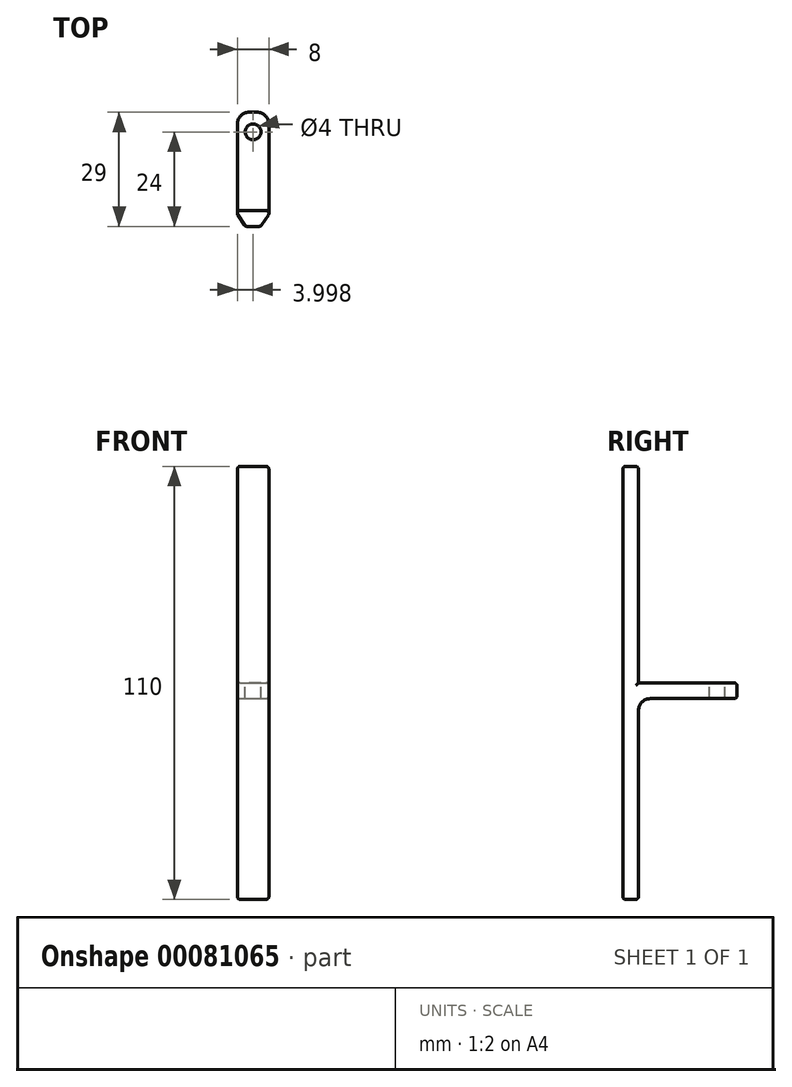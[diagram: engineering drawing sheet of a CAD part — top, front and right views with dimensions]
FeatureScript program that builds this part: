
annotation { "Feature Type Name" : "Feature", "Feature Type Description" : "" }
export const myFeature = defineFeature(function(context is Context, id is Id, definition is map)
    precondition{}
    {
        {
            var Q0;
            Q0=qCreatedBy(makeId("Top.planeOp"),FACE);
            var sketch = newSketch(context, id + "F0", { "sketchPlane" : qUnion([Q0])});
            skLineSegment(sketch, "E0.bottom", {"start": v(-0.33, -0.35) * mm, "end": v(7.67, -0.35) * mm});
            skLineSegment(sketch, "E0.top", {"start": v(-0.33, -4.35) * mm, "end": v(7.67, -4.35) * mm});
            skLineSegment(sketch, "E0.left", {"start": v(-0.33, -0.35) * mm, "end": v(-0.33, -4.35) * mm});
            skLineSegment(sketch, "E0.right", {"start": v(7.67, -0.35) * mm, "end": v(7.67, -4.35) * mm});
            skSolve(sketch);
        }
        {
            var Q0;
            Q0 = qSketchRegion(id + "F0", true);
            extrude(context, id + "F1", {"entities" : qUnion([Q0]), "depth" : 110 * mm});
        }
        {
            var Q0;
            Q0=makeQuery(id+"F1.opExtrude","SWEPT_FACE",FACE,{"disambiguationData":[OSD([sQuery(id+"F0.wireOp",EDGE,"E0.bottom")])]});
            var sketch = newSketch(context, id + "F2", { "sketchPlane" : qUnion([Q0])});
            skLineSegment(sketch, "E1.bottom", {"start": v(0.33, 51) * mm, "end": v(-7.67, 51) * mm});
            skLineSegment(sketch, "E1.top", {"start": v(0.33, 55) * mm, "end": v(-7.67, 55) * mm});
            skLineSegment(sketch, "E1.left", {"start": v(0.33, 51) * mm, "end": v(0.33, 55) * mm});
            skLineSegment(sketch, "E1.right", {"start": v(-7.67, 51) * mm, "end": v(-7.67, 55) * mm});
            skSolve(sketch);
        }
        {
            var Q0;
            Q0 = qSketchRegion(id + "F2", true);
            extrude(context, id + "F3", {"entities" : qUnion([Q0]), "operationType" : NewBodyOperationType.ADD, "depth" : 25 * mm});
        }
        {
            var Q0;
            Q0=makeQuery(id+"F3.opExtrude","SWEPT_FACE",FACE,{"disambiguationData":[OSD([sQuery(id+"F2.wireOp",EDGE,"E1.top")])]});
            var sketch = newSketch(context, id + "F4", { "sketchPlane" : qUnion([Q0])});
            skCircle(sketch, "E2", {"center": v(3.67, 19.65) * mm, "radius": 2 * mm});
            skSolve(sketch);
        }
        {
            var Q0;
            Q0 = qSketchRegion(id + "F4", true);
            extrude(context, id + "F5", {"entities" : qUnion([Q0]), "operationType" : NewBodyOperationType.REMOVE, "endBound" : BoundingType.THROUGH_ALL, "oppositeDirection" : true, "depth" : 25 * mm});
        }
        {
            var Q0;
            Q0=makeQuery(id+"F3.opExtrude","CAP_EDGE",EDGE,{"disambiguationData":[OSD([sQuery(id+"F2.wireOp",EDGE,"E1.top")])],"isStart":true});
            var Q1;
            Q1=makeQuery(id+"F3.opExtrude","CAP_EDGE",EDGE,{"disambiguationData":[OSD([sQuery(id+"F2.wireOp",EDGE,"E1.bottom")])],"isStart":true});
            fillet(context, id + "F6", {"entities" : qUnion([Q0, Q1]), "radius" : 3 * mm, "tangentPropagation" : true, "allowEdgeOverflow" : false});
        }
        {
            var Q0;
            Q0=makeQuery(id+"F1.opExtrude","SWEPT_EDGE",EDGE,{"disambiguationData":[OSD([sQuery(id+"F0.wireOp",EDGE,"E0.top"),sQuery(id+"F0.wireOp",EDGE,"E0.right")])]});
            var Q1;
            Q1=makeQuery(id+"F1.opExtrude","SWEPT_EDGE",EDGE,{"disambiguationData":[OSD([sQuery(id+"F0.wireOp",EDGE,"E0.top"),sQuery(id+"F0.wireOp",EDGE,"E0.left")])]});
            chamfer(context, id + "F7", {"entities" : qUnion([Q0, Q1]), "chamferType" : ChamferType.TWO_OFFSETS, "width1" : 3 * mm, "oppositeDirection" : false, "width2" : 2 * mm, "tangentPropagation" : true});
        }
        {
            var Q0;
            Q0=makeQuery(id+"F3.opExtrude","CAP_EDGE",EDGE,{"disambiguationData":[OSD([sQuery(id+"F2.wireOp",EDGE,"E1.right")])],"isStart":false});
            var Q1;
            Q1=makeQuery(id+"F3.opExtrude","CAP_EDGE",EDGE,{"disambiguationData":[OSD([sQuery(id+"F2.wireOp",EDGE,"E1.left")])],"isStart":false});
            fillet(context, id + "F8", {"entities" : qUnion([Q0, Q1]), "radius" : 3 * mm, "tangentPropagation" : true, "allowEdgeOverflow" : false});
        }
        {
            var Q0;
            Q0=makeQuery(id+"F3.boolean.opBoolean","MERGE",FACE,{"derivedFrom":[makeQuery(id+"F1.opExtrude","SWEPT_FACE",FACE,{"disambiguationData":[OSD([sQuery(id+"F0.wireOp",EDGE,"E0.left")])]}),makeQuery(id+"F3.opExtrude","SWEPT_FACE",FACE,{"disambiguationData":[OSD([sQuery(id+"F2.wireOp",EDGE,"E1.left")])]})]});
            var Q1;
            Q1=makeQuery(id+"F3.boolean.opBoolean","MERGE",FACE,{"derivedFrom":[makeQuery(id+"F1.opExtrude","SWEPT_FACE",FACE,{"disambiguationData":[OSD([sQuery(id+"F0.wireOp",EDGE,"E0.right")])]}),makeQuery(id+"F3.opExtrude","SWEPT_FACE",FACE,{"disambiguationData":[OSD([sQuery(id+"F2.wireOp",EDGE,"E1.right")])]})]});
            var Q2;
            Q2=makeQuery(id+"F1.opExtrude","CAP_FACE",FACE,{"disambiguationData":[OSD([sQuery(id+"F0.wireOp",EDGE,"E0.bottom"),sQuery(id+"F0.wireOp",EDGE,"E0.top"),sQuery(id+"F0.wireOp",EDGE,"E0.left"),sQuery(id+"F0.wireOp",EDGE,"E0.right")])],"isStart":false});
            var Q3;
            Q3=makeQuery(id+"F1.opExtrude","CAP_FACE",FACE,{"disambiguationData":[OSD([sQuery(id+"F0.wireOp",EDGE,"E0.bottom"),sQuery(id+"F0.wireOp",EDGE,"E0.top"),sQuery(id+"F0.wireOp",EDGE,"E0.left"),sQuery(id+"F0.wireOp",EDGE,"E0.right")])],"isStart":true});
            var Q4;
            Q4=makeQuery(id+"F1.opExtrude","SWEPT_FACE",FACE,{"disambiguationData":[OSD([sQuery(id+"F0.wireOp",EDGE,"E0.top")])]});
            fillet(context, id + "F9", {"entities" : qUnion([Q0, Q1, Q2, Q3, Q4]), "radius" : .7 * mm, "tangentPropagation" : true, "allowEdgeOverflow" : false});
        }
    });
